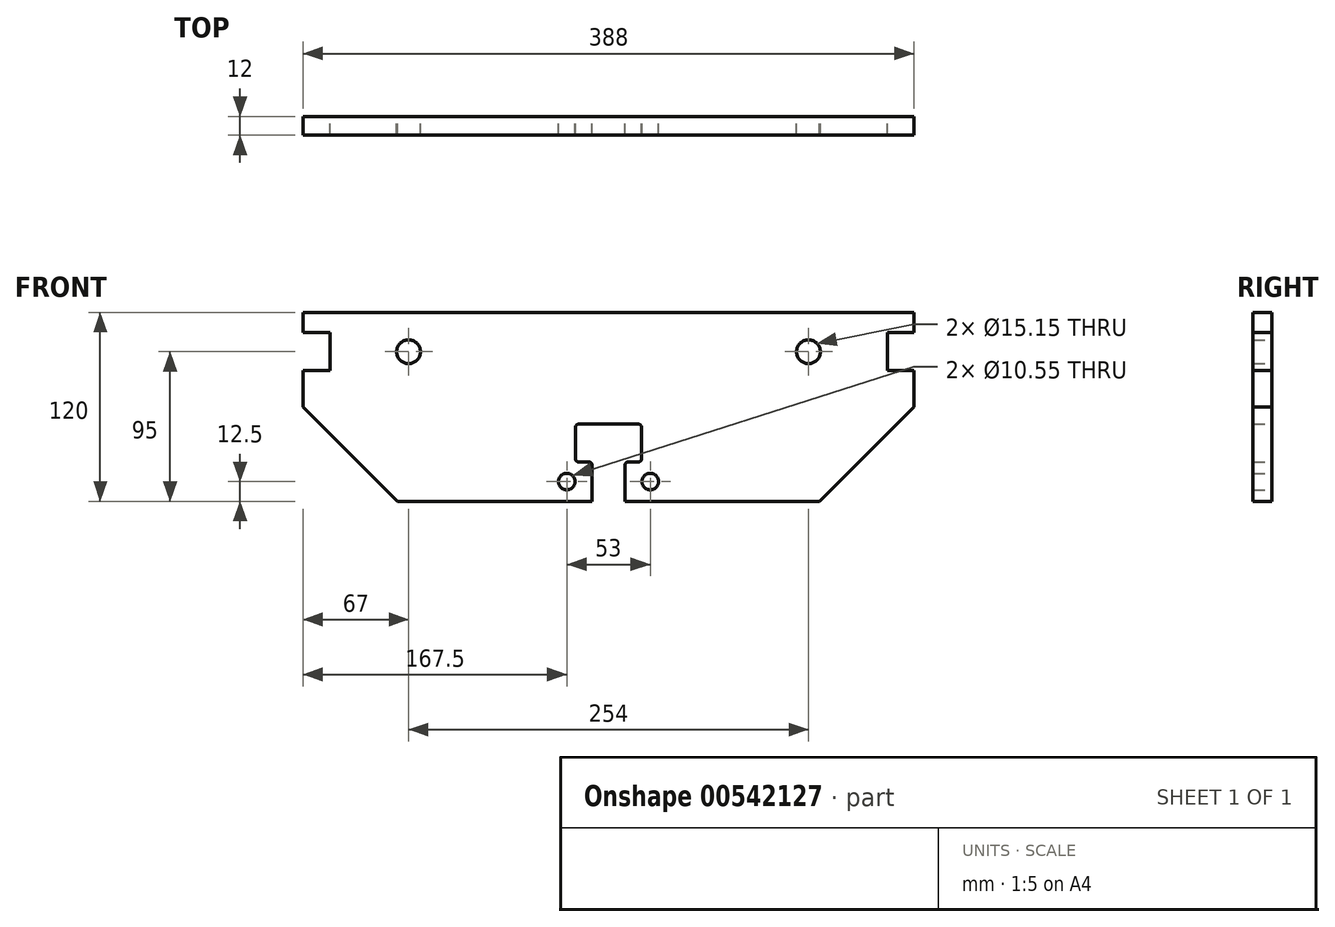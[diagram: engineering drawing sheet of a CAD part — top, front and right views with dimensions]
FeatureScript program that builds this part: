
annotation { "Feature Type Name" : "Feature", "Feature Type Description" : "" }
export const myFeature = defineFeature(function(context is Context, id is Id, definition is map)
    precondition{}
    {
        {
            var Q0;
            Q0=qCreatedBy(makeId("Front.planeOp"),FACE);
            var sketch = newSketch(context, id + "F0", { "sketchPlane" : qUnion([Q0])});
            skLineSegment(sketch, "E0", {"start": v(0, 0) * mm, "end": v(0, -71) * mm});
            skLineSegment(sketch, "E1", {"start": v(0, -71) * mm, "end": v(19, -71) * mm});
            skLineSegment(sketch, "E2", {"start": v(21, -73) * mm, "end": v(21, -93) * mm});
            skLineSegment(sketch, "E3", {"start": v(19, -95) * mm, "end": v(12.5, -95) * mm});
            skLineSegment(sketch, "E4", {"start": v(10.5, -97) * mm, "end": v(10.5, -120) * mm});
            skLineSegment(sketch, "E5", {"start": v(10.5, -120) * mm, "end": v(134, -120) * mm});
            skLineSegment(sketch, "E6", {"start": v(134, -120) * mm, "end": v(194, -60) * mm});
            skLineSegment(sketch, "E7", {"start": v(194, -60) * mm, "end": v(194, -36.86) * mm});
            skLineSegment(sketch, "E8", {"start": v(194, -36.86) * mm, "end": v(177, -36.86) * mm});
            skLineSegment(sketch, "E9", {"start": v(177, -36.86) * mm, "end": v(177, -12.86) * mm});
            skLineSegment(sketch, "E10", {"start": v(177, -12.86) * mm, "end": v(194, -12.86) * mm});
            skLineSegment(sketch, "E11", {"start": v(194, -12.86) * mm, "end": v(194, 0) * mm});
            skLineSegment(sketch, "E12", {"start": v(194, 0) * mm, "end": v(0, 0) * mm});
            skCircle(sketch, "E13", {"center": v(127, -25) * mm, "radius": 7.58 * mm});
            skCircle(sketch, "E14", {"center": v(26.5, -107.5) * mm, "radius": 5.28 * mm});
            skPoint(sketch, "E15.visualSharp", {"position": v(21, -71) * mm});
            skArc(sketch, "E15.filletArc", {"start": v(21, -73) * mm, "mid": v(20.41, -71.59) * mm, "end": v(19, -71) * mm});
            skPoint(sketch, "E16.visualSharp", {"position": v(21, -95) * mm});
            skArc(sketch, "E16.filletArc", {"start": v(19, -95) * mm, "mid": v(20.41, -94.41) * mm, "end": v(21, -93) * mm});
            skPoint(sketch, "E17.visualSharp", {"position": v(10.5, -95) * mm});
            skArc(sketch, "E17.filletArc", {"start": v(12.5, -95) * mm, "mid": v(11.09, -95.59) * mm, "end": v(10.5, -97) * mm});
            skSolve(sketch);
        }
        {
            var Q0;
            Q0=makeQuery(id+"F0.imprint","IMPRINT",FACE,{"disambiguationData":[TD([[makeQuery(id+"F0.imprint","IMPRINT",EDGE,{"derivedFrom":sQuery(id+"F0.wireOp",EDGE,"E0")}),1.0]])]});
            extrude(context, id + "F1", {"entities" : qUnion([Q0]), "depth" : 12 * mm, "offsetDistance" : 25 * mm});
        }
        {
            var Q0;
            Q0=makeQuery(id+"F1.opExtrude","SWEPT_BODY",BODY,{"disambiguationData":[OSD([sQuery(id+"F0.wireOp",EDGE,"E0"),sQuery(id+"F0.wireOp",EDGE,"E1"),sQuery(id+"F0.wireOp",EDGE,"E2"),sQuery(id+"F0.wireOp",EDGE,"E3"),sQuery(id+"F0.wireOp",EDGE,"E4"),sQuery(id+"F0.wireOp",EDGE,"E5"),sQuery(id+"F0.wireOp",EDGE,"E6"),sQuery(id+"F0.wireOp",EDGE,"E7"),sQuery(id+"F0.wireOp",EDGE,"E8"),sQuery(id+"F0.wireOp",EDGE,"E9"),sQuery(id+"F0.wireOp",EDGE,"E10"),sQuery(id+"F0.wireOp",EDGE,"E11"),sQuery(id+"F0.wireOp",EDGE,"E12"),sQuery(id+"F0.wireOp",EDGE,"E13"),sQuery(id+"F0.wireOp",EDGE,"E14"),sQuery(id+"F0.wireOp",EDGE,"E15.filletArc"),sQuery(id+"F0.wireOp",EDGE,"E16.filletArc"),sQuery(id+"F0.wireOp",EDGE,"E17.filletArc")])]});
            var Q1;
            Q1=makeQuery(id+"F1.opExtrude","SWEPT_FACE",FACE,{"disambiguationData":[OSD([sQuery(id+"F0.wireOp",EDGE,"E0")])]});
            mirror(context, id + "F2", {"operationType" : NewBodyOperationType.ADD, "entities" : qUnion([Q0]), "mirrorPlane" : qUnion([Q1])});
        }
    });
